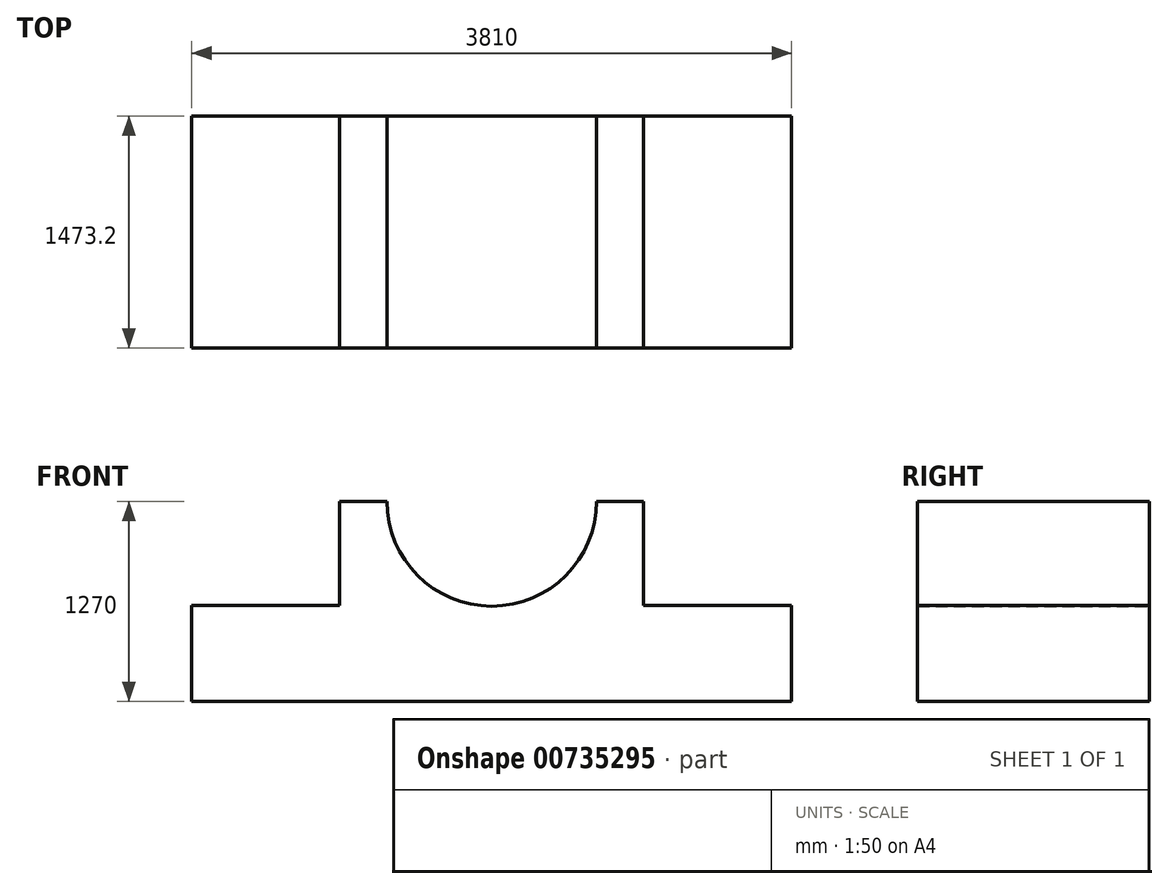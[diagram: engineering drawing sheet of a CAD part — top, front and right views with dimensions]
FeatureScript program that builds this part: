
annotation { "Feature Type Name" : "Feature", "Feature Type Description" : "" }
export const myFeature = defineFeature(function(context is Context, id is Id, definition is map)
    precondition{}
    {
        {
            var Q0;
            Q0=qCreatedBy(makeId("Front.planeOp"),FACE);
            var sketch = newSketch(context, id + "F0", { "sketchPlane" : qUnion([Q0])});
            skLineSegment(sketch, "E0", {"start": v(-73.5, -38.48) * mm, "end": v(3736.5, -38.48) * mm});
            skLineSegment(sketch, "E1", {"start": v(3736.5, -38.48) * mm, "end": v(3736.5, 571.12) * mm});
            skLineSegment(sketch, "E2", {"start": v(-73.5, -38.48) * mm, "end": v(-73.5, 571.12) * mm});
            skLineSegment(sketch, "E3", {"start": v(-73.5, 571.12) * mm, "end": v(866.3, 571.12) * mm});
            skLineSegment(sketch, "E4", {"start": v(866.3, 571.12) * mm, "end": v(866.3, 1231.52) * mm});
            skLineSegment(sketch, "E5", {"start": v(866.3, 1231.52) * mm, "end": v(1171.1, 1231.52) * mm});
            skLineSegment(sketch, "E6", {"start": v(1171.1, 1231.52) * mm, "end": v(1831.5, 1231.52) * mm});
            skLineSegment(sketch, "E7", {"start": v(3736.5, 571.12) * mm, "end": v(2796.7, 571.12) * mm});
            skLineSegment(sketch, "E8", {"start": v(2796.7, 571.12) * mm, "end": v(2796.7, 1231.52) * mm});
            skLineSegment(sketch, "E9", {"start": v(2796.7, 1231.52) * mm, "end": v(2491.9, 1231.52) * mm});
            skCircle(sketch, "E10", {"center": v(1831.5, 1231.52) * mm, "radius": 665.12 * mm});
            skSolve(sketch);
        }
        {
            var Q0;
            Q0=makeQuery(id+"F0.imprint","IMPRINT",FACE,{"disambiguationData":[TD([[makeQuery(id+"F0.imprint","IMPRINT",EDGE,{"derivedFrom":sQuery(id+"F0.wireOp",EDGE,"E0")}),1.0]])]});
            extrude(context, id + "F1", {"entities" : qUnion([Q0]), "depth" : 1473.2 * mm, "offsetDistance" : 25.4 * mm});
        }
    });
